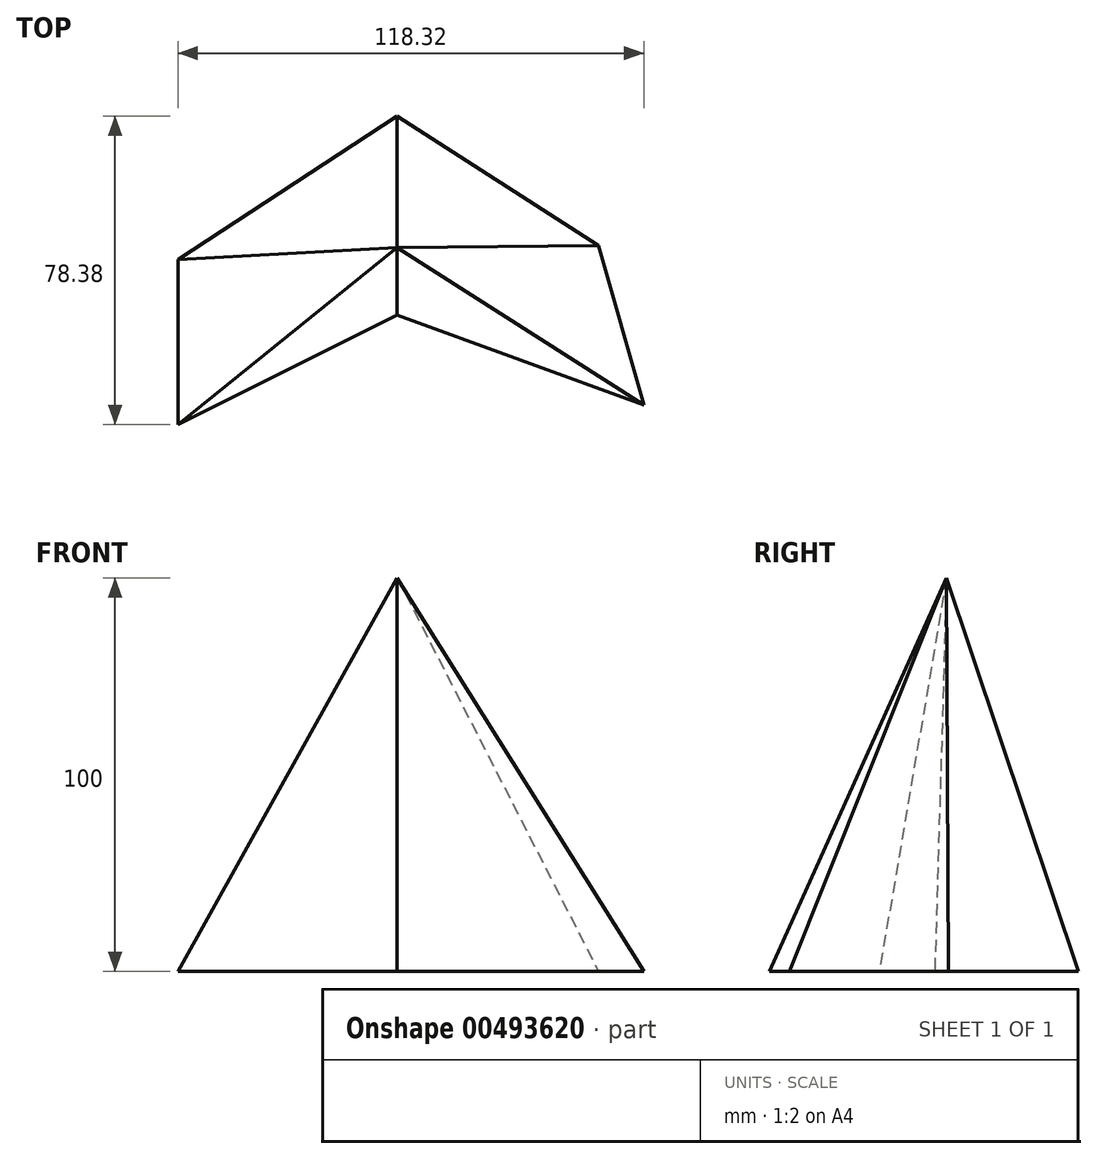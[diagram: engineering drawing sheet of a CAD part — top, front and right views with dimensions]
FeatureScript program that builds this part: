
annotation { "Feature Type Name" : "Feature", "Feature Type Description" : "" }
export const myFeature = defineFeature(function(context is Context, id is Id, definition is map)
    precondition{}
    {
        {
            var Q0;
            Q0=qCreatedBy(makeId("Top.planeOp"),FACE);
            var sketch = newSketch(context, id + "F0", { "sketchPlane" : qUnion([Q0])});
            skLineSegment(sketch, "E0", {"start": v(-55.7, -27.86) * mm, "end": v(-55.7, 14.07) * mm});
            skLineSegment(sketch, "E1", {"start": v(-55.7, 14.07) * mm, "end": v(0, 50.52) * mm});
            skLineSegment(sketch, "E2", {"start": v(0, 50.52) * mm, "end": v(51.14, 17.57) * mm});
            skLineSegment(sketch, "E3", {"start": v(51.14, 17.57) * mm, "end": v(62.62, -22.87) * mm});
            skLineSegment(sketch, "E4", {"start": v(62.62, -22.87) * mm, "end": v(0, 0) * mm});
            skLineSegment(sketch, "E5", {"start": v(0, 0) * mm, "end": v(-55.7, -27.86) * mm});
            skSolve(sketch);
        }
        {
            var Q0;
            Q0=qCreatedBy(makeId("Top.planeOp"),FACE);
            cPlane(context, id + "F1", {"entities" : qUnion([Q0]), "cplaneType" : CPlaneType.OFFSET, "offset" : 100 * mm, "width" : 150 * mm, "height" : 150 * mm});
        }
        {
            var Q0;
            Q0=qCreatedBy(id+"F1.planeOp",FACE);
            var sketch = newSketch(context, id + "F2", { "sketchPlane" : qUnion([Q0])});
            skPoint(sketch, "E6", {"position": v(0, 17.08) * mm});
            skSolve(sketch);
        }
        {
            var Q0;
            Q0=sQuery(id+"F2.wireOp",VERTEX,"E6");
            var Q1;
            Q1=makeQuery(id+"F0.imprint","IMPRINT",FACE,{"disambiguationData":[TD([[makeQuery(id+"F0.imprint","IMPRINT",EDGE,{"derivedFrom":sQuery(id+"F0.wireOp",EDGE,"E0")}),-1.0]])]});
            loft(context, id + "F3", {"sheetProfilesArray" : [{ "sheetProfileEntities" : qUnion([Q0]) }, { "sheetProfileEntities" : qUnion([Q1]) }]});
        }
    });
